# Revit family: URA_Eclairage_de_Securite_URAPROOF
name_source: partatom
category: Luminaires
units: mm (PartAtom-declared; Revit-internal decimal feet)

## family parameters
Cote de connecteur circulaire = Utiliser le diamètre
Couper avec des vides une fois chargée = Non
Hôte = Face
Partagée = Non
Point de calcul de pièce = Non
Source d'éclairage = Oui
Type d'élément = Normal

## types (16) — shared parameters
Angle de l'inclinaison = 60.00°
Condition Générale d'Utilisation = https://export.legrand.com
Elévation par défaut = 1219 mm
Fichier de distribution photométrique = generic
Filtre de couleur = 16777215
Gradation des changements de température de couleur de lampe = <Aucun>
TYPE_DE_MONTAGE = pose murale en saillie

## per-type parameters (varying)
- BAES URAPROOF EVAC S.SATI 55: ADAPTE_AU_TYPE_DE_MARQUAGE=autocollant; ALIMENTATION=décentralisé (batterie individuelle); CATEGORIE_PRODUIT=Autonome; CLASSE_DE_PROTECTION=II; CLASSE_DE_PROTECTION_(IP)=IP55; COULEUR_DU_BOITIER=blanc; DISTANCE_DE_RECONNAISSANCE=15; DUREE_DE_GARANTIE_BAES_COMPLET=4; ETAT_DES_ACCUS=NiCd; FLUX_LUMINEUX_EN_MODE_D'URGENCE=45; FONCTION=Evac; FORMAT_PRODUIT=rectangle; HAUTEUR/PROFONDEUR=55; INSTALLATION_DE_SURVEILLANCE=auto-test automatique; LARGEUR=118; LONGUEUR=239; MATERIAU_DU_BOITIER=plastique; MATERIAU_DU_COUVERCLE=plastique transparent; PUISSANCE_DE_LA_LAMPE=0.6; REFERENCE_ARTICLE=117318; REF_BATTERIE_DE_RECHANGE=111903; RESERVE_DE_MARCHE=1; SOURCE_LUMINEUSE=LED non interchangeable; TENSION_NOMINALE_(MAX)=253; TENSION_NOMINALE_(MIN)=207; TYPE_DE_COMMUTATION=mode veille; TYPE_DE_TENSION=CA
- BAES URAPROOF EVAC ADR 55: ADAPTE_AU_TYPE_DE_MARQUAGE=autocollant; ALIMENTATION=décentralisé (batterie individuelle); CATEGORIE_PRODUIT=Autonome; CLASSE_DE_PROTECTION=II; CLASSE_DE_PROTECTION_(IP)=IP55; COULEUR_DU_BOITIER=blanc; DISTANCE_DE_RECONNAISSANCE=15; DUREE_DE_GARANTIE_BAES_COMPLET=4; ETAT_DES_ACCUS=NiCd; FLUX_LUMINEUX_EN_MODE_D'URGENCE=45; FONCTION=Evac; FORMAT_PRODUIT=rectangle; HAUTEUR/PROFONDEUR=55; INSTALLATION_DE_SURVEILLANCE=auto-test automatique; LARGEUR=118; LONGUEUR=239; MATERIAU_DU_BOITIER=plastique; MATERIAU_DU_COUVERCLE=plastique transparent; PUISSANCE_DE_LA_LAMPE=0.6; REFERENCE_ARTICLE=117319; REF_BATTERIE_DE_RECHANGE=111903; RESERVE_DE_MARCHE=1; SOURCE_LUMINEUSE=LED non interchangeable; TENSION_NOMINALE_(MAX)=253; TENSION_NOMINALE_(MIN)=207; TYPE_DE_COMMUTATION=mode veille; TYPE_DE_TENSION=CA
- BAES URAPROOF EVAC S.SATI 66: ADAPTE_AU_TYPE_DE_MARQUAGE=autocollant; ALIMENTATION=décentralisé (batterie individuelle); CATEGORIE_PRODUIT=Autonome; CLASSE_DE_PROTECTION=II; CLASSE_DE_PROTECTION_(IP)=IP66; COULEUR_DU_BOITIER=blanc; DISTANCE_DE_RECONNAISSANCE=15; DUREE_DE_GARANTIE_BAES_COMPLET=4; ETAT_DES_ACCUS=NiCd; FLUX_LUMINEUX_EN_MODE_D'URGENCE=45; FONCTION=Evac; FORMAT_PRODUIT=rectangle; HAUTEUR/PROFONDEUR=55; INSTALLATION_DE_SURVEILLANCE=auto-test automatique; LARGEUR=118; LONGUEUR=239; MATERIAU_DU_BOITIER=plastique; MATERIAU_DU_COUVERCLE=plastique transparent; PUISSANCE_DE_LA_LAMPE=0.6; REFERENCE_ARTICLE=117418; REF_BATTERIE_DE_RECHANGE=111903; RESERVE_DE_MARCHE=1; SOURCE_LUMINEUSE=LED non interchangeable; TENSION_NOMINALE_(MAX)=253; TENSION_NOMINALE_(MIN)=207; TYPE_DE_COMMUTATION=mode veille; TYPE_DE_TENSION=CA
- BAES URAPROOF EVAC ADR 66: ADAPTE_AU_TYPE_DE_MARQUAGE=autocollant; ALIMENTATION=décentralisé (batterie individuelle); CATEGORIE_PRODUIT=Autonome; CLASSE_DE_PROTECTION=II; CLASSE_DE_PROTECTION_(IP)=IP66; COULEUR_DU_BOITIER=blanc; DISTANCE_DE_RECONNAISSANCE=15; DUREE_DE_GARANTIE_BAES_COMPLET=4; ETAT_DES_ACCUS=NiCd; FLUX_LUMINEUX_EN_MODE_D'URGENCE=45; FONCTION=Evac; FORMAT_PRODUIT=rectangle; HAUTEUR/PROFONDEUR=55; INSTALLATION_DE_SURVEILLANCE=auto-test automatique; LARGEUR=118; LONGUEUR=239; MATERIAU_DU_BOITIER=plastique; MATERIAU_DU_COUVERCLE=plastique transparent; PUISSANCE_DE_LA_LAMPE=0.6; REFERENCE_ARTICLE=117419; REF_BATTERIE_DE_RECHANGE=111903; RESERVE_DE_MARCHE=1; SOURCE_LUMINEUSE=LED non interchangeable; TENSION_NOMINALE_(MAX)=253; TENSION_NOMINALE_(MIN)=207; TYPE_DE_COMMUTATION=mode veille; TYPE_DE_TENSION=CA
- BAES URAPROOF AMB S.SATI 66: ALIMENTATION=décentralisé (batterie individuelle); CATEGORIE_PRODUIT=Autonome; CLASSE_DE_PROTECTION=II; CLASSE_DE_PROTECTION_(IP)=IP66; COULEUR_DU_BOITIER=blanc; DISTANCE_DE_RECONNAISSANCE=15; DUREE_DE_GARANTIE_BAES_COMPLET=4; ETAT_DES_ACCUS=NiMh; FLUX_LUMINEUX_EN_MODE_D'URGENCE=400; FONCTION=Amb; FORMAT_PRODUIT=rectangle; HAUTEUR/PROFONDEUR=57; INSTALLATION_DE_SURVEILLANCE=auto-test automatique; LARGEUR=164; LONGUEUR=261; MATERIAU_DU_BOITIER=plastique; MATERIAU_DU_COUVERCLE=plastique transparent; PUISSANCE_DE_LA_LAMPE=4; REFERENCE_ARTICLE=117428; REF_BATTERIE_DE_RECHANGE=111904+111905; RESERVE_DE_MARCHE=1; SOURCE_LUMINEUSE=LED non interchangeable; TENSION_NOMINALE_(MAX)=253; TENSION_NOMINALE_(MIN)=207; TYPE_DE_COMMUTATION=mode veille; TYPE_DE_TENSION=CA
- BAES URAPROOF AMB ADR 66: ALIMENTATION=décentralisé (batterie individuelle); CATEGORIE_PRODUIT=Autonome; CLASSE_DE_PROTECTION=II; CLASSE_DE_PROTECTION_(IP)=IP66; COULEUR_DU_BOITIER=blanc; DISTANCE_DE_RECONNAISSANCE=15; DUREE_DE_GARANTIE_BAES_COMPLET=4; ETAT_DES_ACCUS=NiMh; FLUX_LUMINEUX_EN_MODE_D'URGENCE=400; FONCTION=Amb; FORMAT_PRODUIT=rectangle; HAUTEUR/PROFONDEUR=57; INSTALLATION_DE_SURVEILLANCE=auto-test automatique; LARGEUR=164; LONGUEUR=261; MATERIAU_DU_BOITIER=plastique; MATERIAU_DU_COUVERCLE=plastique transparent; PUISSANCE_DE_LA_LAMPE=6.6; REFERENCE_ARTICLE=117429; REF_BATTERIE_DE_RECHANGE=111904+111905; RESERVE_DE_MARCHE=1; SOURCE_LUMINEUSE=LED non interchangeable; TENSION_NOMINALE_(MAX)=253; TENSION_NOMINALE_(MIN)=207; TYPE_DE_COMMUTATION=mode veille; TYPE_DE_TENSION=CA
- BAEH URAPROOF ADR 66: ADAPTE_AU_TYPE_DE_MARQUAGE=autocollant; ALIMENTATION=décentralisé (batterie individuelle); CATEGORIE_PRODUIT=Autonome; CLASSE_DE_PROTECTION=II; CLASSE_DE_PROTECTION_(IP)=IP66; COULEUR_DU_BOITIER=blanc; DISTANCE_DE_RECONNAISSANCE=15; DUREE_DE_GARANTIE_BAES_COMPLET=4; ETAT_DES_ACCUS=NiCd; FLUX_LUMINEUX_EN_MODE_D'URGENCE=8; FONCTION=BAEH; FORMAT_PRODUIT=rectangle; HAUTEUR/PROFONDEUR=55; INSTALLATION_DE_SURVEILLANCE=auto-test automatique; LARGEUR=118; LONGUEUR=239; MATERIAU_DU_BOITIER=plastique; MATERIAU_DU_COUVERCLE=plastique transparent; PUISSANCE_DE_LA_LAMPE=0.04; REFERENCE_ARTICLE=117438; REF_BATTERIE_DE_RECHANGE=111903; RESERVE_DE_MARCHE=5; SOURCE_LUMINEUSE=LED non interchangeable; TENSION_NOMINALE_(MAX)=253; TENSION_NOMINALE_(MIN)=207; TYPE_DE_COMMUTATION=mode veille; TYPE_DE_TENSION=CA
- BAES AMB PERMANENT SATI ADR 66: ALIMENTATION=décentralisé (batterie individuelle); CATEGORIE_PRODUIT=Autonome; CLASSE_DE_PROTECTION=II; CLASSE_DE_PROTECTION_(IP)=IP66; COULEUR_DU_BOITIER=blanc; DISTANCE_DE_RECONNAISSANCE=15; DUREE_DE_GARANTIE_BAES_COMPLET=2; ETAT_DES_ACCUS=NiMh; FLUX_LUMINEUX_EN_MODE_D'URGENCE=450; FONCTION=Amb; FORMAT_PRODUIT=rectangle; HAUTEUR/PROFONDEUR=57; INSTALLATION_DE_SURVEILLANCE=auto-test automatique; LARGEUR=164; LONGUEUR=261; MATERIAU_DU_BOITIER=plastique; MATERIAU_DU_COUVERCLE=plastique transparent; PUISSANCE_DE_LA_LAMPE=6; REFERENCE_ARTICLE=117439; REF_BATTERIE_DE_RECHANGE=111904+111905; RESERVE_DE_MARCHE=1; SOURCE_LUMINEUSE=LED non interchangeable; TENSION_NOMINALE_(MAX)=253; TENSION_NOMINALE_(MIN)=207; TYPE_DE_COMMUTATION=mode veille; TYPE_DE_TENSION=CA
- BAES + BAEH URAPROOF ADR 66: ADAPTE_AU_TYPE_DE_MARQUAGE=autocollant; ALIMENTATION=décentralisé (batterie individuelle); CATEGORIE_PRODUIT=Autonome; CLASSE_DE_PROTECTION=II; CLASSE_DE_PROTECTION_(IP)=IP66; COULEUR_DU_BOITIER=blanc; DISTANCE_DE_RECONNAISSANCE=15; DUREE_DE_GARANTIE_BAES_COMPLET=4; ETAT_DES_ACCUS=NiCd; FLUX_LUMINEUX_EN_MODE_D'URGENCE=45; FONCTION=BAES+BAEH; FORMAT_PRODUIT=rectangle; HAUTEUR/PROFONDEUR=55; INSTALLATION_DE_SURVEILLANCE=auto-test automatique; LARGEUR=118; LONGUEUR=239; MATERIAU_DU_BOITIER=plastique; MATERIAU_DU_COUVERCLE=plastique transparent; PUISSANCE_DE_LA_LAMPE=0.8; REFERENCE_ARTICLE=117448; REF_BATTERIE_DE_RECHANGE=2*111903; RESERVE_DE_MARCHE=1; SOURCE_LUMINEUSE=LED non interchangeable; TENSION_NOMINALE_(MAX)=253; TENSION_NOMINALE_(MIN)=207; TYPE_DE_COMMUTATION=mode veille; TYPE_DE_TENSION=CA
- BAES + DBR URAPROOF SATI: ADAPTE_AU_TYPE_DE_MARQUAGE=autocollant; ALIMENTATION=décentralisé (batterie individuelle); CATEGORIE_PRODUIT=Autonome; CLASSE_DE_PROTECTION=II; CLASSE_DE_PROTECTION_(IP)=IP66; COULEUR_DU_BOITIER=blanc; DISTANCE_DE_RECONNAISSANCE=15; DUREE_DE_GARANTIE_BAES_COMPLET=4; ETAT_DES_ACCUS=NiCd; FLUX_LUMINEUX_EN_MODE_D'URGENCE=45; FONCTION=DBR; FORMAT_PRODUIT=rectangle; HAUTEUR/PROFONDEUR=57; INSTALLATION_DE_SURVEILLANCE=auto-test automatique; LARGEUR=164; LONGUEUR=261; MATERIAU_DU_BOITIER=plastique; MATERIAU_DU_COUVERCLE=plastique transparent; PUISSANCE_DE_LA_LAMPE=1; REFERENCE_ARTICLE=117457; REF_BATTERIE_DE_RECHANGE=111903; RESERVE_DE_MARCHE=1; SOURCE_LUMINEUSE=LED non interchangeable; TENSION_NOMINALE_(MAX)=253; TENSION_NOMINALE_(MIN)=207; TYPE_DE_COMMUTATION=mode veille; TYPE_DE_TENSION=CA
- URAPROOF DBR ADR: ADAPTE_AU_TYPE_DE_MARQUAGE=autocollant; ALIMENTATION=central (batterie centrale); CATEGORIE_PRODUIT=Autonome; CLASSE_DE_PROTECTION=II; CLASSE_DE_PROTECTION_(IP)=IP55; COULEUR_DU_BOITIER=blanc; DUREE_DE_GARANTIE_BAES_COMPLET=4; ETAT_DES_ACCUS=NiCd; FLUX_LUMINEUX_EN_MODE_D'URGENCE=45; FONCTION=DBR; FORMAT_PRODUIT=rectangle; HAUTEUR/PROFONDEUR=164.5; INSTALLATION_DE_SURVEILLANCE=auto-test automatique; LARGEUR=57; LONGUEUR=261; MATERIAU_DU_BOITIER=plastique; MATERIAU_DU_COUVERCLE=verre transparent; PUISSANCE_DE_LA_LAMPE=4.5; REFERENCE_ARTICLE=117459; REF_BATTERIE_DE_RECHANGE=111903; RESERVE_DE_MARCHE=1; SOURCE_LUMINEUSE=LED non interchangeable; TENSION_NOMINALE_(MAX)=253; TENSION_NOMINALE_(MIN)=207; TYPE_DE_COMMUTATION=circuit permanent/circuit de secours; TYPE_DE_TENSION=CA
- LSC URAPROOF EVAC 110/220/230: ADAPTE_AU_TYPE_DE_MARQUAGE=autocollant; ALIMENTATION=central (batterie centrale); CATEGORIE_PRODUIT=LSC; CLASSE_DE_PROTECTION=II; CLASSE_DE_PROTECTION_(IP)=IP55; COULEUR_DU_BOITIER=blanc; DISTANCE_DE_RECONNAISSANCE=15; DUREE_DE_GARANTIE_BAES_COMPLET=4; ETAT_DES_ACCUS=non applicable; FLUX_LUMINEUX_EN_MODE_D'URGENCE=45; FONCTION=Evac; FORMAT_PRODUIT=rectangle; HAUTEUR/PROFONDEUR=57; INSTALLATION_DE_SURVEILLANCE=auto-test automatique; LARGEUR=164.5; LONGUEUR=261.2; MATERIAU_DU_BOITIER=plastique; MATERIAU_DU_COUVERCLE=plastique transparent; PUISSANCE_DE_LA_LAMPE=0.8; REFERENCE_ARTICLE=127314; SOURCE_LUMINEUSE=LED non interchangeable; TENSION_NOMINALE_(MAX)=230; TENSION_NOMINALE_(MIN)=110; TYPE_DE_COMMUTATION=circuit permanent/circuit de secours; TYPE_DE_TENSION=CA/CC
- LSC URAPROOF EVAC 24/48 IP 66: ADAPTE_AU_TYPE_DE_MARQUAGE=autocollant; ALIMENTATION=central (batterie centrale); CATEGORIE_PRODUIT=LSC; CLASSE_DE_PROTECTION=II; CLASSE_DE_PROTECTION_(IP)=IP66; COULEUR_DU_BOITIER=blanc; DISTANCE_DE_RECONNAISSANCE=15; DUREE_DE_GARANTIE_BAES_COMPLET=4; ETAT_DES_ACCUS=non applicable; FLUX_LUMINEUX_EN_MODE_D'URGENCE=45; FONCTION=Evac; FORMAT_PRODUIT=rectangle; HAUTEUR/PROFONDEUR=57; INSTALLATION_DE_SURVEILLANCE=auto-test automatique; LARGEUR=164.5; LONGUEUR=261.2; MATERIAU_DU_BOITIER=plastique; MATERIAU_DU_COUVERCLE=plastique transparent; PUISSANCE_DE_LA_LAMPE=0.8; REFERENCE_ARTICLE=127215; SOURCE_LUMINEUSE=LED non interchangeable; TENSION_NOMINALE_(MAX)=48; TENSION_NOMINALE_(MIN)=24; TYPE_DE_COMMUTATION=circuit permanent/circuit de secours; TYPE_DE_TENSION=CC
- LSC URAPROOF AMB 110/220/230: ALIMENTATION=central (batterie centrale); CATEGORIE_PRODUIT=LSC; CLASSE_DE_PROTECTION=II; CLASSE_DE_PROTECTION_(IP)=IP66; COULEUR_DU_BOITIER=blanc; DISTANCE_DE_RECONNAISSANCE=15; DUREE_DE_GARANTIE_BAES_COMPLET=4; ETAT_DES_ACCUS=non applicable; FLUX_LUMINEUX_EN_MODE_D'URGENCE=400; FONCTION=Amb; FORMAT_PRODUIT=rectangle; HAUTEUR/PROFONDEUR=57; INSTALLATION_DE_SURVEILLANCE=auto-test automatique; LARGEUR=164.5; LONGUEUR=261.2; MATERIAU_DU_BOITIER=plastique; MATERIAU_DU_COUVERCLE=plastique transparent; PUISSANCE_DE_LA_LAMPE=6.6; REFERENCE_ARTICLE=127224; SOURCE_LUMINEUSE=LED non interchangeable; TENSION_NOMINALE_(MAX)=230; TENSION_NOMINALE_(MIN)=110; TYPE_DE_COMMUTATION=circuit permanent/circuit de secours; TYPE_DE_TENSION=CA/CC
- LSC URAPROOF AMB 24/48: ALIMENTATION=central (batterie centrale); CATEGORIE_PRODUIT=LSC; CLASSE_DE_PROTECTION=II; CLASSE_DE_PROTECTION_(IP)=IP66; COULEUR_DU_BOITIER=blanc; DISTANCE_DE_RECONNAISSANCE=15; DUREE_DE_GARANTIE_BAES_COMPLET=4; ETAT_DES_ACCUS=non applicable; FLUX_LUMINEUX_EN_MODE_D'URGENCE=400; FONCTION=Amb; FORMAT_PRODUIT=rectangle; HAUTEUR/PROFONDEUR=57; INSTALLATION_DE_SURVEILLANCE=auto-test automatique; LARGEUR=164.5; LONGUEUR=261.2; MATERIAU_DU_BOITIER=plastique; MATERIAU_DU_COUVERCLE=plastique transparent; PUISSANCE_DE_LA_LAMPE=6.6; REFERENCE_ARTICLE=127225; SOURCE_LUMINEUSE=LED non interchangeable; TENSION_NOMINALE_(MAX)=48; TENSION_NOMINALE_(MIN)=24; TYPE_DE_COMMUTATION=circuit permanent/circuit de secours; TYPE_DE_TENSION=CC
- LSC URAPROOF EVAC 24/48 IP 55: CATEGORIE_PRODUIT=LSC; CLASSE_DE_PROTECTION_(IP)=24; COULEUR_DU_BOITIER=0.8; DIAMETRE_EXTERNE=164.5; DISTANCE_DE_RECONNAISSANCE=45; DUREE_DE_GARANTIE_BAES_COMPLET=4; ETAT_DES_ACCUS=plastique transparent; FLUX_LUMINEUX_EN_MODE_D'URGENCE=auto-test automatique; FONCTION=Evac; FORMAT_PRODUIT=15; HAUTEUR/PROFONDEUR=261.2; INSTALLATION_DE_SURVEILLANCE=IP55; LARGEUR=II; LARGEUR_DE_MONTAGE=central (batterie centrale); LONGUEUR=autocollant; LONGUEUR_D'ENCASTREMENT=circuit permanent/circuit de secours; MATERIAU_DU_BOITIER=57; REFERENCE_ARTICLE=127315; REF_BATTERIE_DE_RECHANGE=rectangle; RESERVE_DE_MARCHE=CC; SOURCE_LUMINEUSE=plastique; TENSION_NOMINALE_(MAX)=non applicable; TENSION_NOMINALE_(MIN)=48; TYPE_DE_COMMUTATION=LED non interchangeable; TYPE_DE_TENSION=blanc

note: column(s) folded — value = type name in every type: DESIGNATION_ARTICLE
